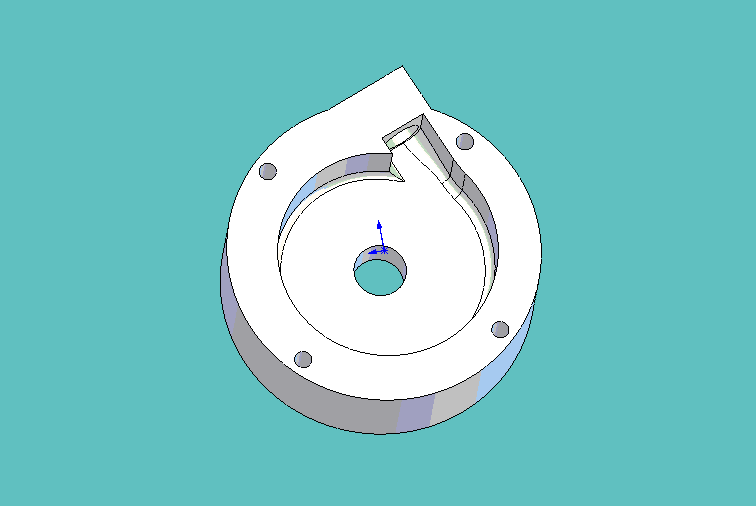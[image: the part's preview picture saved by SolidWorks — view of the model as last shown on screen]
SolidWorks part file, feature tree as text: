
SOLIDWORKS PART (.sldprt)
format: sldprt  version: not decoded by parser v0  size: 766,976 bytes
history: native  units: mm
features: sketch x7, extrude x2, cut_extrude x2, material x1, helix x1, hole x1, fillet x1 (+13 scaffold rows collapsed)
feature tree (28):
  scaffold x13  (default folders/planes/origin — collapsed)
  material  "Material <not specified>"
  sketch  "Sketch1"  dims[D1=0.0mm]
  helix  "Helix/Spiral1"  Pitch=5mm
  sketch  "Sketch3"  dims[c1.D3=~36.070819mm c1.D2=50.0mm c1.D4=50.0mm c2.D3=50.0mm c2.D2=10.0mm c3.D3=30.0mm c3.D2=18.0mm c4.D3=~15.208157mm c4.D4=25.0mm c4.D5=~13.687265mm c5.D3=15.0mm c5.D2=15.6mm c5.D4=21.6mm c5.D5=3.0mm c5.D6=~3.673503mm c6.D4=30.0mm c6.D6=~3.380416mm c7.D4=3.0mm c7.D6=~28.014445mm c8.D4=28.0mm c8.D6=~16.897538mm c8.D1=0.0mm c8.D2=15.0mm c9.D1=0.0mm c9.D4=10.0mm c10.D1=0.0mm c10.D5=3.0mm c10.D6=3.0mm]
  extrude  "Extrude1"  Depth=34mm
  cut_extrude  "Cut-Extrude2"  [1 undecoded]
  sketch  "Sketch3<6>"  dims[D1=20.0mm]
  extrude  "Extrude6"  [1 undecoded]
  sketch  "Sketch3<7>"
  hole  "M16.75 (16.75) Diameter Hole1"  Diameter=16.75mm Depth=34mm
  sketch  "Sketch21"
  sketch  "Sketch20"  dims[hole-wizard template sketch: 59 standard entries collapsed; hole parameters kept: c18.Thru Hole Dia.=16.75mm c18.Thru Hole Depth=34.0mm]
  sketch  "Sketch22"  dims[D1=13.6mm D2=8.0mm]
  cut_extrude  "Cut-Extrude3"  Depth=3mm
  fillet  "Fillet1"  Radius=3mm
decode coverage: 10 of 14 modeling features carry decoded parameters
note: ~ marks probable driven/reference dimensions
note: 2 parameter values undecoded
note: suppression state not decoded; provenance and decode notes live in map.json
